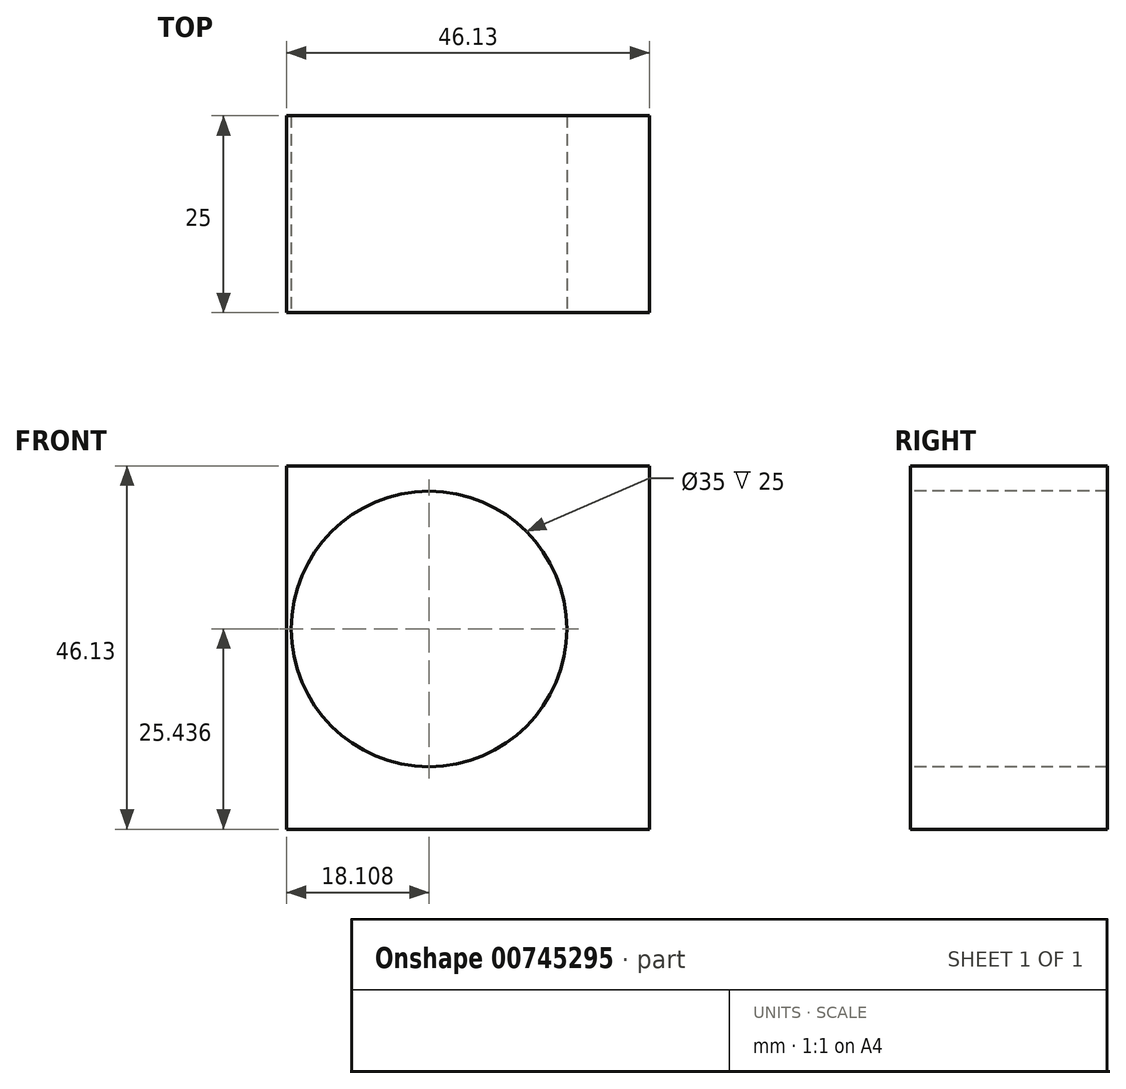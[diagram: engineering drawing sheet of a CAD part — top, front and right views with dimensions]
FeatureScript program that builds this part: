
annotation { "Feature Type Name" : "Feature", "Feature Type Description" : "" }
export const myFeature = defineFeature(function(context is Context, id is Id, definition is map)
    precondition{}
    {
        {
            var Q0;
            Q0=qCreatedBy(makeId("Front.planeOp"),FACE);
            var sketch = newSketch(context, id + "F0", { "sketchPlane" : qUnion([Q0])});
            skLineSegment(sketch, "E0.bottom", {"start": v(0, 0) * mm, "end": v(-46.13, 0) * mm});
            skLineSegment(sketch, "E0.top", {"start": v(0, 46.13) * mm, "end": v(-46.13, 46.13) * mm});
            skLineSegment(sketch, "E0.left", {"start": v(0, 0) * mm, "end": v(0, 46.13) * mm});
            skLineSegment(sketch, "E0.right", {"start": v(-46.13, 0) * mm, "end": v(-46.13, 46.13) * mm});
            skSolve(sketch);
        }
        {
            var Q0;
            Q0=makeQuery(id+"F0.imprint","IMPRINT",FACE,{"disambiguationData":[TD([[makeQuery(id+"F0.imprint","IMPRINT",EDGE,{"derivedFrom":sQuery(id+"F0.wireOp",EDGE,"E0.bottom")}),-1.0]])]});
            extrude(context, id + "F1", {"entities" : qUnion([Q0]), "oppositeDirection" : true, "depth" : 25 * mm, "offsetDistance" : 25 * mm});
        }
        {
            var Q0;
            Q0=makeQuery(id+"F1.opExtrude","CAP_FACE",FACE,{"disambiguationData":[OSD([sQuery(id+"F0.wireOp",EDGE,"E0.bottom"),sQuery(id+"F0.wireOp",EDGE,"E0.top"),sQuery(id+"F0.wireOp",EDGE,"E0.left"),sQuery(id+"F0.wireOp",EDGE,"E0.right")])],"isStart":true});
            var sketch = newSketch(context, id + "F2", { "sketchPlane" : qUnion([Q0])});
            skCircle(sketch, "E1", {"center": v(-28.02, 25.44) * mm, "radius": 10.86 * mm});
            skSolve(sketch);
        }
        {
            var Q0;
            Q0=sQuery(id+"F2.wireOp",VERTEX,"E1.center");
            var Q1;
            Q1=makeQuery(id+"F1.opExtrude","SWEPT_BODY",BODY,{"disambiguationData":[OSD([sQuery(id+"F0.wireOp",EDGE,"E0.bottom"),sQuery(id+"F0.wireOp",EDGE,"E0.top"),sQuery(id+"F0.wireOp",EDGE,"E0.left"),sQuery(id+"F0.wireOp",EDGE,"E0.right")])]});
            hole(context, id + "F3", {"style" : HoleStyle.SIMPLE, "endStyle" : HoleEndStyle.THROUGH, "holeDiameter" : 35 * mm, "majorDiameter" : 5 * mm, "isTappedThrough" : true, "tappedDepth" : 12 * mm, "tapClearance" : 3, "locations" : qUnion([Q0]), "scope" : qUnion([Q1])});
        }
    });
